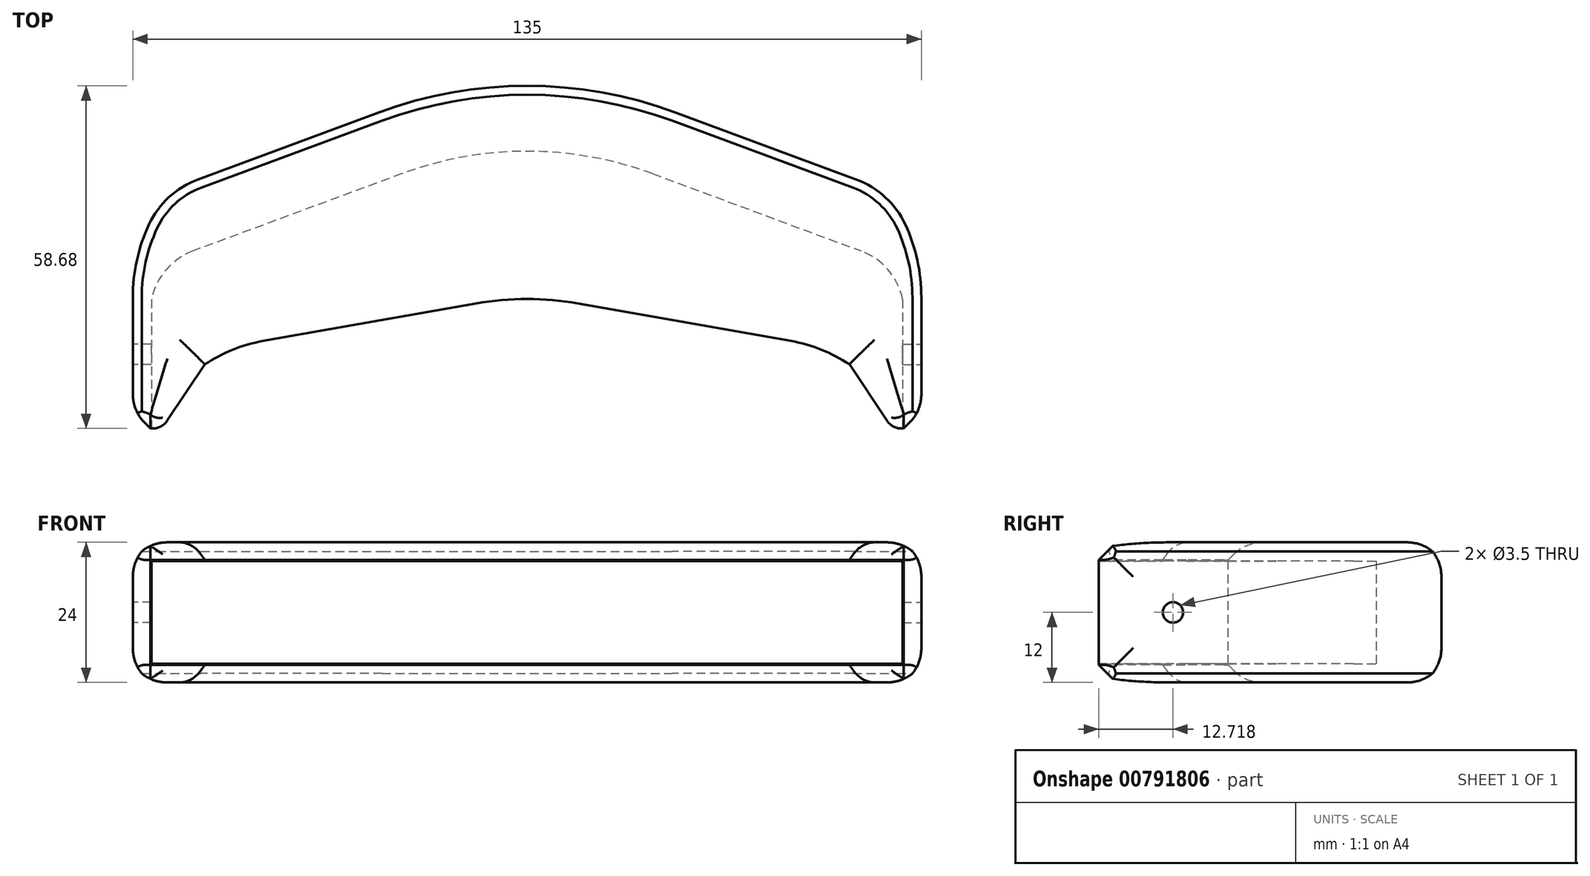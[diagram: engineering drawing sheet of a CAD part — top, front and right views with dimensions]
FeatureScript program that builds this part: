
annotation { "Feature Type Name" : "Feature", "Feature Type Description" : "" }
export const myFeature = defineFeature(function(context is Context, id is Id, definition is map)
    precondition{}
    {
        {
            var Q0;
            Q0=qCreatedBy(makeId("Top.planeOp"),FACE);
            var sketch = newSketch(context, id + "F0", { "sketchPlane" : qUnion([Q0])});
            skLineSegment(sketch, "E0.left", {"start": v(-67.5, -4.63) * mm, "end": v(-67.5, -27.07) * mm});
            skLineSegment(sketch, "E0.right", {"start": v(67.5, -4.63) * mm, "end": v(67.5, -27.07) * mm});
            skLineSegment(sketch, "E1", {"start": v(-22.58, 19.56) * mm, "end": v(-58.22, 6.36) * mm});
            skLineSegment(sketch, "E2", {"start": v(22.58, 19.56) * mm, "end": v(58.25, 6.35) * mm});
            skPoint(sketch, "E3.visualSharp", {"position": v(-67.5, 2.93) * mm});
            skPoint(sketch, "E4.visualSharp", {"position": v(67.5, 2.93) * mm});
            skPoint(sketch, "E5.visualSharp", {"position": v(0, 27.93) * mm});
            skArc(sketch, "E5.filletArc", {"start": v(22.58, 19.56) * mm, "mid": v(0, 23.61) * mm, "end": v(-22.58, 19.56) * mm});
            skLineSegment(sketch, "E6", {"start": v(-67.5, -27.07) * mm, "end": v(-64.1, -27.07) * mm});
            skLineSegment(sketch, "E7", {"start": v(-61.6, -25.74) * mm, "end": v(-55.17, -16.09) * mm});
            skLineSegment(sketch, "E8", {"start": v(67.5, -27.07) * mm, "end": v(64.1, -27.07) * mm});
            skLineSegment(sketch, "E9", {"start": v(61.6, -25.74) * mm, "end": v(55.17, -16.09) * mm});
            skPoint(sketch, "E10.visualSharp", {"position": v(-52.5, -12.08) * mm});
            skPoint(sketch, "E11.visualSharp", {"position": v(52.5, -12.08) * mm});
            skPoint(sketch, "E12.visualSharp", {"position": v(62.5, -27.07) * mm});
            skArc(sketch, "E12.filletArc", {"start": v(61.6, -25.74) * mm, "mid": v(62.69, -26.72) * mm, "end": v(64.1, -27.07) * mm});
            skPoint(sketch, "E13.visualSharp", {"position": v(-62.5, -27.07) * mm});
            skArc(sketch, "E13.filletArc", {"start": v(-64.1, -27.07) * mm, "mid": v(-62.69, -26.72) * mm, "end": v(-61.6, -25.74) * mm});
            skLineSegment(sketch, "E14", {"start": v(-45.18, -12.08) * mm, "end": v(-8.66, -5.66) * mm});
            skLineSegment(sketch, "E15", {"start": v(8.66, -5.66) * mm, "end": v(45.18, -12.08) * mm});
            skPoint(sketch, "E16.visualSharp", {"position": v(0, -4.13) * mm});
            skArc(sketch, "E16.filletArc", {"start": v(8.66, -5.66) * mm, "mid": v(0, -4.9) * mm, "end": v(-8.66, -5.66) * mm});
            skPoint(sketch, "E17.visualSharp", {"position": v(-63.32, 13.1) * mm});
            skPoint(sketch, "E18.visualSharp", {"position": v(58.32, 13.1) * mm});
            skArc(sketch, "E19", {"start": v(-58.22, 6.36) * mm, "mid": v(-64.3, 2.09) * mm, "end": v(-67.5, -4.63) * mm});
            skArc(sketch, "E20", {"start": v(67.5, -4.63) * mm, "mid": v(64.32, 2.08) * mm, "end": v(58.25, 6.35) * mm});
            skArc(sketch, "E21", {"start": v(-45.18, -12.08) * mm, "mid": v(-50.39, -13.57) * mm, "end": v(-55.17, -16.09) * mm});
            skArc(sketch, "E22", {"start": v(55.17, -16.09) * mm, "mid": v(50.39, -13.57) * mm, "end": v(45.18, -12.08) * mm});
            skPoint(sketch, "E23.visualSharp", {"position": v(-61, 13.86) * mm});
            skPoint(sketch, "E24.visualSharp", {"position": v(61.03, 13.85) * mm});
            skSolve(sketch);
        }
        {
            var Q0;
            Q0 = qSketchRegion(id + "F0", true);
            extrude(context, id + "F1", {"entities" : qUnion([Q0]), "depth" : 24 * mm, "offsetDistance" : 25 * mm});
        }
        {
            var Q0;
            Q0=makeQuery(id+"F1.opExtrude","SWEPT_FACE",FACE,{"disambiguationData":[OSD([sQuery(id+"F0.wireOp",EDGE,"E14")])]});
            var Q1;
            Q1=makeQuery(id+"F1.opExtrude","SWEPT_FACE",FACE,{"disambiguationData":[OSD([sQuery(id+"F0.wireOp",EDGE,"E16.filletArc")])]});
            var Q2;
            Q2=makeQuery(id+"F1.opExtrude","SWEPT_FACE",FACE,{"disambiguationData":[OSD([sQuery(id+"F0.wireOp",EDGE,"E15")])]});
            var Q3;
            Q3=makeQuery(id+"F1.opExtrude","SWEPT_FACE",FACE,{"disambiguationData":[OSD([sQuery(id+"F0.wireOp",EDGE,"E11.filletArc")])]});
            var Q4;
            Q4=makeQuery(id+"F1.opExtrude","SWEPT_FACE",FACE,{"disambiguationData":[OSD([sQuery(id+"F0.wireOp",EDGE,"E9")])]});
            var Q5;
            Q5=makeQuery(id+"F1.opExtrude","SWEPT_FACE",FACE,{"disambiguationData":[OSD([sQuery(id+"F0.wireOp",EDGE,"E12.filletArc")])]});
            var Q6;
            Q6=makeQuery(id+"F1.opExtrude","SWEPT_FACE",FACE,{"disambiguationData":[OSD([sQuery(id+"F0.wireOp",EDGE,"E7")])]});
            var Q7;
            Q7=makeQuery(id+"F1.opExtrude","SWEPT_FACE",FACE,{"disambiguationData":[OSD([sQuery(id+"F0.wireOp",EDGE,"E10.filletArc")])]});
            var Q8;
            Q8=makeQuery(id+"F1.opExtrude","SWEPT_FACE",FACE,{"disambiguationData":[OSD([sQuery(id+"F0.wireOp",EDGE,"E13.filletArc")])]});
            var Q9;
            Q9=makeQuery(id+"F1.opExtrude","SWEPT_FACE",FACE,{"disambiguationData":[OSD([sQuery(id+"F0.wireOp",EDGE,"E6")])]});
            var Q10;
            Q10=makeQuery(id+"F1.opExtrude","SWEPT_FACE",FACE,{"disambiguationData":[OSD([sQuery(id+"F0.wireOp",EDGE,"E8")])]});
            var Q11;
            Q11=makeQuery(id+"F1.opExtrude","SWEPT_FACE",FACE,{"disambiguationData":[OSD([sQuery(id+"F0.wireOp",EDGE,"E21")])]});
            var Q12;
            Q12=makeQuery(id+"F1.opExtrude","SWEPT_FACE",FACE,{"disambiguationData":[OSD([sQuery(id+"F0.wireOp",EDGE,"E22")])]});
            shell(context, id + "F2", {"entities" : qUnion([Q0, Q1, Q2, Q3, Q4, Q5, Q6, Q7, Q8, Q9, Q10, Q11, Q12]), "thickness" : 3.2 * mm});
        }
        {
            var Q0;
            Q0=makeQuery(id+"F1.opExtrude","CAP_FACE",FACE,{"disambiguationData":[OSD([sQuery(id+"F0.wireOp",EDGE,"E0.left"),sQuery(id+"F0.wireOp",EDGE,"E0.right"),sQuery(id+"F0.wireOp",EDGE,"E1"),sQuery(id+"F0.wireOp",EDGE,"E2"),sQuery(id+"F0.wireOp",EDGE,"E3.filletArc"),sQuery(id+"F0.wireOp",EDGE,"E4.filletArc"),sQuery(id+"F0.wireOp",EDGE,"E5.filletArc"),sQuery(id+"F0.wireOp",EDGE,"E6"),sQuery(id+"F0.wireOp",EDGE,"E7"),sQuery(id+"F0.wireOp",EDGE,"E8"),sQuery(id+"F0.wireOp",EDGE,"E9"),sQuery(id+"F0.wireOp",EDGE,"E10.filletArc"),sQuery(id+"F0.wireOp",EDGE,"E11.filletArc"),sQuery(id+"F0.wireOp",EDGE,"E12.filletArc"),sQuery(id+"F0.wireOp",EDGE,"E13.filletArc"),sQuery(id+"F0.wireOp",EDGE,"E14"),sQuery(id+"F0.wireOp",EDGE,"E15"),sQuery(id+"F0.wireOp",EDGE,"E16.filletArc")])],"isStart":false});
            var sketch = newSketch(context, id + "F3", { "sketchPlane" : qUnion([Q0])});
            skLineSegment(sketch, "E25.0", {"start": v(-25.35, 27.07) * mm, "end": v(-56.35, 15.59) * mm});
            skArc(sketch, "E25.1", {"start": v(25.35, 27.07) * mm, "mid": v(0, 31.61) * mm, "end": v(-25.35, 27.07) * mm});
            skLineSegment(sketch, "E25.2", {"start": v(25.35, 27.07) * mm, "end": v(56.36, 15.58) * mm});
            skArc(sketch, "E26", {"start": v(-64.73, 7.86) * mm, "mid": v(-66.8, 1.77) * mm, "end": v(-67.5, -4.63) * mm});
            skArc(sketch, "E27", {"start": v(67.5, -4.63) * mm, "mid": v(66.8, 1.74) * mm, "end": v(64.76, 7.82) * mm});
            skArc(sketch, "E28.filletArc", {"start": v(-56.35, 15.59) * mm, "mid": v(-61.3, 12.55) * mm, "end": v(-64.73, 7.86) * mm});
            skArc(sketch, "E29.filletArc", {"start": v(64.76, 7.82) * mm, "mid": v(61.33, 12.53) * mm, "end": v(56.36, 15.58) * mm});
            skLineSegment(sketch, "E30", {"start": v(-22.58, 19.56) * mm, "end": v(-58.22, 6.36) * mm});
            skLineSegment(sketch, "E31", {"start": v(22.58, 19.56) * mm, "end": v(58.25, 6.35) * mm});
            skArc(sketch, "E32.filletArc", {"start": v(22.58, 19.56) * mm, "mid": v(0, 23.61) * mm, "end": v(-22.58, 19.56) * mm});
            skArc(sketch, "E33", {"start": v(-58.22, 6.36) * mm, "mid": v(-64.3, 2.09) * mm, "end": v(-67.5, -4.63) * mm});
            skArc(sketch, "E34", {"start": v(67.5, -4.63) * mm, "mid": v(64.32, 2.08) * mm, "end": v(58.25, 6.35) * mm});
            skSolve(sketch);
        }
        {
            var Q0;
            Q0 = qSketchRegion(id + "F3", true);
            extrude(context, id + "F4", {"entities" : qUnion([Q0]), "operationType" : NewBodyOperationType.ADD, "oppositeDirection" : true, "depth" : 24 * mm, "offsetDistance" : 25 * mm});
        }
        {
            var Q0;
            Q0=makeQuery(id+"F4.boolean.opBoolean","MERGE",FACE,{"derivedFrom":[makeQuery(id+"F1.opExtrude","CAP_FACE",FACE,{"disambiguationData":[OSD([sQuery(id+"F0.wireOp",EDGE,"E0.left"),sQuery(id+"F0.wireOp",EDGE,"E0.right"),sQuery(id+"F0.wireOp",EDGE,"E1"),sQuery(id+"F0.wireOp",EDGE,"E2"),sQuery(id+"F0.wireOp",EDGE,"E3.filletArc"),sQuery(id+"F0.wireOp",EDGE,"E4.filletArc"),sQuery(id+"F0.wireOp",EDGE,"E5.filletArc"),sQuery(id+"F0.wireOp",EDGE,"E6"),sQuery(id+"F0.wireOp",EDGE,"E7"),sQuery(id+"F0.wireOp",EDGE,"E8"),sQuery(id+"F0.wireOp",EDGE,"E9"),sQuery(id+"F0.wireOp",EDGE,"E10.filletArc"),sQuery(id+"F0.wireOp",EDGE,"E11.filletArc"),sQuery(id+"F0.wireOp",EDGE,"E12.filletArc"),sQuery(id+"F0.wireOp",EDGE,"E13.filletArc"),sQuery(id+"F0.wireOp",EDGE,"E14"),sQuery(id+"F0.wireOp",EDGE,"E15"),sQuery(id+"F0.wireOp",EDGE,"E16.filletArc")])],"isStart":false}),makeQuery(id+"F4.opExtrude","CAP_FACE",FACE,{"disambiguationData":[OSD([sQuery(id+"F3.wireOp",EDGE,"276efb32-5cb6-4f63-bdc1-496fc01c60db.2"),sQuery(id+"F3.wireOp",EDGE,"276efb32-5cb6-4f63-bdc1-496fc01c60db.3"),sQuery(id+"F3.wireOp",EDGE,"276efb32-5cb6-4f63-bdc1-496fc01c60db.4"),sQuery(id+"F3.wireOp",EDGE,"0241c868-49d8-4b9a-ac46-58dfbb5efc39"),sQuery(id+"F3.wireOp",EDGE,"348bde47-0a47-42e3-8267-499f4a5522ae"),sQuery(id+"F3.wireOp",EDGE,"215ec280-f68a-4f47-a865-032d440a2936.filletArc"),sQuery(id+"F3.wireOp",EDGE,"fd759fa0-5ab4-4b6e-8cb0-b494d0b887aa.filletArc"),sQuery(id+"F3.wireOp",EDGE,"73b2d2fd-a5d6-4b7d-9539-ec2af92cbbd5"),sQuery(id+"F3.wireOp",EDGE,"2c1b0ead-8098-4b90-8860-aa6a1cb84409"),sQuery(id+"F3.wireOp",EDGE,"515ed680-fa81-4fbc-94c5-9d26c9a30982.filletArc"),sQuery(id+"F3.wireOp",EDGE,"67b69344-5ccb-49e4-9dbe-6815e7e981bc.filletArc"),sQuery(id+"F3.wireOp",EDGE,"a765c2de-9442-403f-932b-7ea1a12a6cac.filletArc")])],"isStart":true})]});
            var Q1;
            Q1=makeQuery(id+"F4.boolean.opBoolean","MERGE",FACE,{"derivedFrom":[makeQuery(id+"F1.opExtrude","CAP_FACE",FACE,{"disambiguationData":[OSD([sQuery(id+"F0.wireOp",EDGE,"E0.left"),sQuery(id+"F0.wireOp",EDGE,"E0.right"),sQuery(id+"F0.wireOp",EDGE,"E1"),sQuery(id+"F0.wireOp",EDGE,"E2"),sQuery(id+"F0.wireOp",EDGE,"E3.filletArc"),sQuery(id+"F0.wireOp",EDGE,"E4.filletArc"),sQuery(id+"F0.wireOp",EDGE,"E5.filletArc"),sQuery(id+"F0.wireOp",EDGE,"E6"),sQuery(id+"F0.wireOp",EDGE,"E7"),sQuery(id+"F0.wireOp",EDGE,"E8"),sQuery(id+"F0.wireOp",EDGE,"E9"),sQuery(id+"F0.wireOp",EDGE,"E10.filletArc"),sQuery(id+"F0.wireOp",EDGE,"E11.filletArc"),sQuery(id+"F0.wireOp",EDGE,"E12.filletArc"),sQuery(id+"F0.wireOp",EDGE,"E13.filletArc"),sQuery(id+"F0.wireOp",EDGE,"E14"),sQuery(id+"F0.wireOp",EDGE,"E15"),sQuery(id+"F0.wireOp",EDGE,"E16.filletArc")])],"isStart":true}),makeQuery(id+"F4.opExtrude","CAP_FACE",FACE,{"disambiguationData":[OSD([sQuery(id+"F3.wireOp",EDGE,"276efb32-5cb6-4f63-bdc1-496fc01c60db.2"),sQuery(id+"F3.wireOp",EDGE,"276efb32-5cb6-4f63-bdc1-496fc01c60db.3"),sQuery(id+"F3.wireOp",EDGE,"276efb32-5cb6-4f63-bdc1-496fc01c60db.4"),sQuery(id+"F3.wireOp",EDGE,"0241c868-49d8-4b9a-ac46-58dfbb5efc39"),sQuery(id+"F3.wireOp",EDGE,"348bde47-0a47-42e3-8267-499f4a5522ae"),sQuery(id+"F3.wireOp",EDGE,"215ec280-f68a-4f47-a865-032d440a2936.filletArc"),sQuery(id+"F3.wireOp",EDGE,"fd759fa0-5ab4-4b6e-8cb0-b494d0b887aa.filletArc"),sQuery(id+"F3.wireOp",EDGE,"73b2d2fd-a5d6-4b7d-9539-ec2af92cbbd5"),sQuery(id+"F3.wireOp",EDGE,"2c1b0ead-8098-4b90-8860-aa6a1cb84409"),sQuery(id+"F3.wireOp",EDGE,"515ed680-fa81-4fbc-94c5-9d26c9a30982.filletArc"),sQuery(id+"F3.wireOp",EDGE,"67b69344-5ccb-49e4-9dbe-6815e7e981bc.filletArc"),sQuery(id+"F3.wireOp",EDGE,"a765c2de-9442-403f-932b-7ea1a12a6cac.filletArc")])],"isStart":false})]});
            var Q2;
            Q2=makeQuery(id+"F1.opExtrude","SWEPT_EDGE",EDGE,{"disambiguationData":[OSD([sQuery(id+"F0.wireOp",EDGE,"E0.left"),sQuery(id+"F0.wireOp",EDGE,"E6")])]});
            var Q3;
            Q3=makeQuery(id+"F1.opExtrude","SWEPT_EDGE",EDGE,{"disambiguationData":[OSD([sQuery(id+"F0.wireOp",EDGE,"E0.right"),sQuery(id+"F0.wireOp",EDGE,"E8")])]});
            chamfer(context, id + "F5", {"entities" : qUnion([Q0, Q1, Q2, Q3]), "width" : 3 * mm, "tangentPropagation" : true});
        }
        {
            var Q0;
            Q0=makeQuery(id+"F1.opExtrude","SWEPT_FACE",FACE,{"disambiguationData":[OSD([sQuery(id+"F0.wireOp",EDGE,"E0.left")])]});
            var sketch = newSketch(context, id + "F6", { "sketchPlane" : qUnion([Q0])});
            skCircle(sketch, "E35", {"center": v(14.35, 12) * mm, "radius": 1.75 * mm});
            skPoint(sketch, "E36", {"position": v(14.35, 21) * mm});
            skPoint(sketch, "E37", {"position": v(24.07, 12) * mm});
            skSolve(sketch);
        }
        {
            var Q0;
            Q0 = qSketchRegion(id + "F6", true);
            extrude(context, id + "F7", {"entities" : qUnion([Q0]), "operationType" : NewBodyOperationType.REMOVE, "oppositeDirection" : true, "depth" : 5 * mm, "offsetDistance" : 25 * mm});
        }
        {
            var Q0;
            Q0=makeQuery(id+"F1.opExtrude","SWEPT_FACE",FACE,{"disambiguationData":[OSD([sQuery(id+"F0.wireOp",EDGE,"E0.right")])]});
            var sketch = newSketch(context, id + "F8", { "sketchPlane" : qUnion([Q0])});
            skCircle(sketch, "E38", {"center": v(-14.35, 12) * mm, "radius": 1.75 * mm});
            skPoint(sketch, "E39", {"position": v(-14.35, 21) * mm});
            skPoint(sketch, "E40", {"position": v(-24.07, 12) * mm});
            skSolve(sketch);
        }
        {
            var Q0;
            Q0 = qSketchRegion(id + "F8", true);
            extrude(context, id + "F9", {"entities" : qUnion([Q0]), "operationType" : NewBodyOperationType.REMOVE, "oppositeDirection" : true, "depth" : 5 * mm, "offsetDistance" : 25 * mm});
        }
        {
            var Q0;
            {var subQ0=sQuery(id+"F3.wireOp",EDGE,"E25.1");Q0=makeQuery(id+"F5.opChamfer","BLEND_EDGE",EDGE,{"blendedFrom":[makeQuery(id+"F4.opExtrude","CAP_EDGE",EDGE,{"disambiguationData":[OSD([subQ0])],"isStart":false}),makeQuery(id+"F4.opExtrude","SWEPT_FACE",FACE,{"disambiguationData":[OSD([subQ0])]})],"blendedInto":[makeQuery(id+"F4.opExtrude","SWEPT_FACE",FACE,{"disambiguationData":[OSD([subQ0])]})]});}
            var Q1;
            {var subQ0=sQuery(id+"F3.wireOp",EDGE,"E25.1");Q1=makeQuery(id+"F5.opChamfer","BLEND_EDGE",EDGE,{"blendedFrom":[makeQuery(id+"F4.opExtrude","CAP_EDGE",EDGE,{"disambiguationData":[OSD([subQ0])],"isStart":false}),makeQuery(id+"F4.boolean.opBoolean","MERGE",FACE,{"derivedFrom":[makeQuery(id+"F1.opExtrude","CAP_FACE",FACE,{"disambiguationData":[OSD([sQuery(id+"F0.wireOp",EDGE,"E0.left"),sQuery(id+"F0.wireOp",EDGE,"E0.right"),sQuery(id+"F0.wireOp",EDGE,"E1"),sQuery(id+"F0.wireOp",EDGE,"E2"),sQuery(id+"F0.wireOp",EDGE,"E5.filletArc"),sQuery(id+"F0.wireOp",EDGE,"E6"),sQuery(id+"F0.wireOp",EDGE,"E7"),sQuery(id+"F0.wireOp",EDGE,"E8"),sQuery(id+"F0.wireOp",EDGE,"E9"),sQuery(id+"F0.wireOp",EDGE,"E12.filletArc"),sQuery(id+"F0.wireOp",EDGE,"E13.filletArc"),sQuery(id+"F0.wireOp",EDGE,"E14"),sQuery(id+"F0.wireOp",EDGE,"E15"),sQuery(id+"F0.wireOp",EDGE,"E16.filletArc"),sQuery(id+"F0.wireOp",EDGE,"E19"),sQuery(id+"F0.wireOp",EDGE,"E20"),sQuery(id+"F0.wireOp",EDGE,"E21"),sQuery(id+"F0.wireOp",EDGE,"E22")])],"isStart":true}),makeQuery(id+"F4.opExtrude","CAP_FACE",FACE,{"disambiguationData":[OSD([sQuery(id+"F3.wireOp",EDGE,"E25.0"),subQ0,sQuery(id+"F3.wireOp",EDGE,"E25.2"),sQuery(id+"F3.wireOp",EDGE,"E26"),sQuery(id+"F3.wireOp",EDGE,"E27"),sQuery(id+"F3.wireOp",EDGE,"E28.filletArc"),sQuery(id+"F3.wireOp",EDGE,"E29.filletArc"),sQuery(id+"F3.wireOp",EDGE,"E30"),sQuery(id+"F3.wireOp",EDGE,"E31"),sQuery(id+"F3.wireOp",EDGE,"E32.filletArc"),sQuery(id+"F3.wireOp",EDGE,"E33"),sQuery(id+"F3.wireOp",EDGE,"E34")])],"isStart":false})]})],"blendedInto":[makeQuery(id+"F4.boolean.opBoolean","MERGE",FACE,{"derivedFrom":[makeQuery(id+"F1.opExtrude","CAP_FACE",FACE,{"disambiguationData":[OSD([sQuery(id+"F0.wireOp",EDGE,"E0.left"),sQuery(id+"F0.wireOp",EDGE,"E0.right"),sQuery(id+"F0.wireOp",EDGE,"E1"),sQuery(id+"F0.wireOp",EDGE,"E2"),sQuery(id+"F0.wireOp",EDGE,"E5.filletArc"),sQuery(id+"F0.wireOp",EDGE,"E6"),sQuery(id+"F0.wireOp",EDGE,"E7"),sQuery(id+"F0.wireOp",EDGE,"E8"),sQuery(id+"F0.wireOp",EDGE,"E9"),sQuery(id+"F0.wireOp",EDGE,"E12.filletArc"),sQuery(id+"F0.wireOp",EDGE,"E13.filletArc"),sQuery(id+"F0.wireOp",EDGE,"E14"),sQuery(id+"F0.wireOp",EDGE,"E15"),sQuery(id+"F0.wireOp",EDGE,"E16.filletArc"),sQuery(id+"F0.wireOp",EDGE,"E19"),sQuery(id+"F0.wireOp",EDGE,"E20"),sQuery(id+"F0.wireOp",EDGE,"E21"),sQuery(id+"F0.wireOp",EDGE,"E22")])],"isStart":true}),makeQuery(id+"F4.opExtrude","CAP_FACE",FACE,{"disambiguationData":[OSD([sQuery(id+"F3.wireOp",EDGE,"E25.0"),subQ0,sQuery(id+"F3.wireOp",EDGE,"E25.2"),sQuery(id+"F3.wireOp",EDGE,"E26"),sQuery(id+"F3.wireOp",EDGE,"E27"),sQuery(id+"F3.wireOp",EDGE,"E28.filletArc"),sQuery(id+"F3.wireOp",EDGE,"E29.filletArc"),sQuery(id+"F3.wireOp",EDGE,"E30"),sQuery(id+"F3.wireOp",EDGE,"E31"),sQuery(id+"F3.wireOp",EDGE,"E32.filletArc"),sQuery(id+"F3.wireOp",EDGE,"E33"),sQuery(id+"F3.wireOp",EDGE,"E34")])],"isStart":false})]})]});}
            var Q2;
            {var subQ0=sQuery(id+"F3.wireOp",EDGE,"E25.0");Q2=makeQuery(id+"F5.opChamfer","BLEND_EDGE",EDGE,{"blendedFrom":[makeQuery(id+"F4.opExtrude","CAP_EDGE",EDGE,{"disambiguationData":[OSD([subQ0])],"isStart":true}),makeQuery(id+"F4.boolean.opBoolean","MERGE",FACE,{"derivedFrom":[makeQuery(id+"F1.opExtrude","CAP_FACE",FACE,{"disambiguationData":[OSD([sQuery(id+"F0.wireOp",EDGE,"E0.left"),sQuery(id+"F0.wireOp",EDGE,"E0.right"),sQuery(id+"F0.wireOp",EDGE,"E1"),sQuery(id+"F0.wireOp",EDGE,"E2"),sQuery(id+"F0.wireOp",EDGE,"E5.filletArc"),sQuery(id+"F0.wireOp",EDGE,"E6"),sQuery(id+"F0.wireOp",EDGE,"E7"),sQuery(id+"F0.wireOp",EDGE,"E8"),sQuery(id+"F0.wireOp",EDGE,"E9"),sQuery(id+"F0.wireOp",EDGE,"E12.filletArc"),sQuery(id+"F0.wireOp",EDGE,"E13.filletArc"),sQuery(id+"F0.wireOp",EDGE,"E14"),sQuery(id+"F0.wireOp",EDGE,"E15"),sQuery(id+"F0.wireOp",EDGE,"E16.filletArc"),sQuery(id+"F0.wireOp",EDGE,"E19"),sQuery(id+"F0.wireOp",EDGE,"E20"),sQuery(id+"F0.wireOp",EDGE,"E21"),sQuery(id+"F0.wireOp",EDGE,"E22")])],"isStart":false}),makeQuery(id+"F4.opExtrude","CAP_FACE",FACE,{"disambiguationData":[OSD([subQ0,sQuery(id+"F3.wireOp",EDGE,"E25.1"),sQuery(id+"F3.wireOp",EDGE,"E25.2"),sQuery(id+"F3.wireOp",EDGE,"E26"),sQuery(id+"F3.wireOp",EDGE,"E27"),sQuery(id+"F3.wireOp",EDGE,"E28.filletArc"),sQuery(id+"F3.wireOp",EDGE,"E29.filletArc"),sQuery(id+"F3.wireOp",EDGE,"E30"),sQuery(id+"F3.wireOp",EDGE,"E31"),sQuery(id+"F3.wireOp",EDGE,"E32.filletArc"),sQuery(id+"F3.wireOp",EDGE,"E33"),sQuery(id+"F3.wireOp",EDGE,"E34")])],"isStart":true})]})],"blendedInto":[makeQuery(id+"F4.boolean.opBoolean","MERGE",FACE,{"derivedFrom":[makeQuery(id+"F1.opExtrude","CAP_FACE",FACE,{"disambiguationData":[OSD([sQuery(id+"F0.wireOp",EDGE,"E0.left"),sQuery(id+"F0.wireOp",EDGE,"E0.right"),sQuery(id+"F0.wireOp",EDGE,"E1"),sQuery(id+"F0.wireOp",EDGE,"E2"),sQuery(id+"F0.wireOp",EDGE,"E5.filletArc"),sQuery(id+"F0.wireOp",EDGE,"E6"),sQuery(id+"F0.wireOp",EDGE,"E7"),sQuery(id+"F0.wireOp",EDGE,"E8"),sQuery(id+"F0.wireOp",EDGE,"E9"),sQuery(id+"F0.wireOp",EDGE,"E12.filletArc"),sQuery(id+"F0.wireOp",EDGE,"E13.filletArc"),sQuery(id+"F0.wireOp",EDGE,"E14"),sQuery(id+"F0.wireOp",EDGE,"E15"),sQuery(id+"F0.wireOp",EDGE,"E16.filletArc"),sQuery(id+"F0.wireOp",EDGE,"E19"),sQuery(id+"F0.wireOp",EDGE,"E20"),sQuery(id+"F0.wireOp",EDGE,"E21"),sQuery(id+"F0.wireOp",EDGE,"E22")])],"isStart":false}),makeQuery(id+"F4.opExtrude","CAP_FACE",FACE,{"disambiguationData":[OSD([subQ0,sQuery(id+"F3.wireOp",EDGE,"E25.1"),sQuery(id+"F3.wireOp",EDGE,"E25.2"),sQuery(id+"F3.wireOp",EDGE,"E26"),sQuery(id+"F3.wireOp",EDGE,"E27"),sQuery(id+"F3.wireOp",EDGE,"E28.filletArc"),sQuery(id+"F3.wireOp",EDGE,"E29.filletArc"),sQuery(id+"F3.wireOp",EDGE,"E30"),sQuery(id+"F3.wireOp",EDGE,"E31"),sQuery(id+"F3.wireOp",EDGE,"E32.filletArc"),sQuery(id+"F3.wireOp",EDGE,"E33"),sQuery(id+"F3.wireOp",EDGE,"E34")])],"isStart":true})]})]});}
            var Q3;
            {var subQ0=sQuery(id+"F3.wireOp",EDGE,"E25.0");Q3=makeQuery(id+"F5.opChamfer","BLEND_EDGE",EDGE,{"blendedFrom":[makeQuery(id+"F4.opExtrude","CAP_EDGE",EDGE,{"disambiguationData":[OSD([subQ0])],"isStart":true}),makeQuery(id+"F4.opExtrude","SWEPT_FACE",FACE,{"disambiguationData":[OSD([subQ0])]})],"blendedInto":[makeQuery(id+"F4.opExtrude","SWEPT_FACE",FACE,{"disambiguationData":[OSD([subQ0])]})]});}
            var Q4;
            {var subQ0=sQuery(id+"F0.wireOp",EDGE,"E0.right");Q4=makeQuery(id+"F5.opChamfer","BLEND_EDGE",EDGE,{"blendedFrom":[makeQuery(id+"F1.opExtrude","SWEPT_EDGE",EDGE,{"disambiguationData":[OSD([subQ0,sQuery(id+"F0.wireOp",EDGE,"E8")])]}),makeQuery(id+"F1.opExtrude","SWEPT_FACE",FACE,{"disambiguationData":[OSD([subQ0])]})],"blendedInto":[makeQuery(id+"F1.opExtrude","SWEPT_FACE",FACE,{"disambiguationData":[OSD([subQ0])]})]});}
            var Q5;
            {var subQ0=sQuery(id+"F0.wireOp",EDGE,"E0.left");Q5=makeQuery(id+"F5.opChamfer","BLEND_EDGE",EDGE,{"blendedFrom":[makeQuery(id+"F1.opExtrude","SWEPT_EDGE",EDGE,{"disambiguationData":[OSD([subQ0,sQuery(id+"F0.wireOp",EDGE,"E6")])]}),makeQuery(id+"F1.opExtrude","SWEPT_FACE",FACE,{"disambiguationData":[OSD([subQ0])]})],"blendedInto":[makeQuery(id+"F1.opExtrude","SWEPT_FACE",FACE,{"disambiguationData":[OSD([subQ0])]})]});}
            var Q6;
            {var subQ0=sQuery(id+"F0.wireOp",EDGE,"E15");Q6=makeQuery(id+"F5.opChamfer","BLEND_EDGE",EDGE,{"blendedFrom":[makeQuery(id+"F1.opExtrude","CAP_EDGE",EDGE,{"disambiguationData":[OSD([subQ0])],"isStart":false}),makeQuery(id+"F4.boolean.opBoolean","MERGE",FACE,{"derivedFrom":[makeQuery(id+"F1.opExtrude","CAP_FACE",FACE,{"disambiguationData":[OSD([sQuery(id+"F0.wireOp",EDGE,"E0.left"),sQuery(id+"F0.wireOp",EDGE,"E0.right"),sQuery(id+"F0.wireOp",EDGE,"E1"),sQuery(id+"F0.wireOp",EDGE,"E2"),sQuery(id+"F0.wireOp",EDGE,"E5.filletArc"),sQuery(id+"F0.wireOp",EDGE,"E6"),sQuery(id+"F0.wireOp",EDGE,"E7"),sQuery(id+"F0.wireOp",EDGE,"E8"),sQuery(id+"F0.wireOp",EDGE,"E9"),sQuery(id+"F0.wireOp",EDGE,"E12.filletArc"),sQuery(id+"F0.wireOp",EDGE,"E13.filletArc"),sQuery(id+"F0.wireOp",EDGE,"E14"),subQ0,sQuery(id+"F0.wireOp",EDGE,"E16.filletArc"),sQuery(id+"F0.wireOp",EDGE,"E19"),sQuery(id+"F0.wireOp",EDGE,"E20"),sQuery(id+"F0.wireOp",EDGE,"E21"),sQuery(id+"F0.wireOp",EDGE,"E22")])],"isStart":false}),makeQuery(id+"F4.opExtrude","CAP_FACE",FACE,{"disambiguationData":[OSD([sQuery(id+"F3.wireOp",EDGE,"E25.0"),sQuery(id+"F3.wireOp",EDGE,"E25.1"),sQuery(id+"F3.wireOp",EDGE,"E25.2"),sQuery(id+"F3.wireOp",EDGE,"E26"),sQuery(id+"F3.wireOp",EDGE,"E27"),sQuery(id+"F3.wireOp",EDGE,"E28.filletArc"),sQuery(id+"F3.wireOp",EDGE,"E29.filletArc"),sQuery(id+"F3.wireOp",EDGE,"E30"),sQuery(id+"F3.wireOp",EDGE,"E31"),sQuery(id+"F3.wireOp",EDGE,"E32.filletArc"),sQuery(id+"F3.wireOp",EDGE,"E33"),sQuery(id+"F3.wireOp",EDGE,"E34")])],"isStart":true})]})],"blendedInto":[makeQuery(id+"F4.boolean.opBoolean","MERGE",FACE,{"derivedFrom":[makeQuery(id+"F1.opExtrude","CAP_FACE",FACE,{"disambiguationData":[OSD([sQuery(id+"F0.wireOp",EDGE,"E0.left"),sQuery(id+"F0.wireOp",EDGE,"E0.right"),sQuery(id+"F0.wireOp",EDGE,"E1"),sQuery(id+"F0.wireOp",EDGE,"E2"),sQuery(id+"F0.wireOp",EDGE,"E5.filletArc"),sQuery(id+"F0.wireOp",EDGE,"E6"),sQuery(id+"F0.wireOp",EDGE,"E7"),sQuery(id+"F0.wireOp",EDGE,"E8"),sQuery(id+"F0.wireOp",EDGE,"E9"),sQuery(id+"F0.wireOp",EDGE,"E12.filletArc"),sQuery(id+"F0.wireOp",EDGE,"E13.filletArc"),sQuery(id+"F0.wireOp",EDGE,"E14"),subQ0,sQuery(id+"F0.wireOp",EDGE,"E16.filletArc"),sQuery(id+"F0.wireOp",EDGE,"E19"),sQuery(id+"F0.wireOp",EDGE,"E20"),sQuery(id+"F0.wireOp",EDGE,"E21"),sQuery(id+"F0.wireOp",EDGE,"E22")])],"isStart":false}),makeQuery(id+"F4.opExtrude","CAP_FACE",FACE,{"disambiguationData":[OSD([sQuery(id+"F3.wireOp",EDGE,"E25.0"),sQuery(id+"F3.wireOp",EDGE,"E25.1"),sQuery(id+"F3.wireOp",EDGE,"E25.2"),sQuery(id+"F3.wireOp",EDGE,"E26"),sQuery(id+"F3.wireOp",EDGE,"E27"),sQuery(id+"F3.wireOp",EDGE,"E28.filletArc"),sQuery(id+"F3.wireOp",EDGE,"E29.filletArc"),sQuery(id+"F3.wireOp",EDGE,"E30"),sQuery(id+"F3.wireOp",EDGE,"E31"),sQuery(id+"F3.wireOp",EDGE,"E32.filletArc"),sQuery(id+"F3.wireOp",EDGE,"E33"),sQuery(id+"F3.wireOp",EDGE,"E34")])],"isStart":true})]})]});}
            var Q7;
            {var subQ0=sQuery(id+"F0.wireOp",EDGE,"E9");Q7=makeQuery(id+"F5.opChamfer","BLEND_EDGE",EDGE,{"blendedFrom":[makeQuery(id+"F1.opExtrude","CAP_EDGE",EDGE,{"disambiguationData":[OSD([subQ0])],"isStart":false}),makeQuery(id+"F4.boolean.opBoolean","MERGE",FACE,{"derivedFrom":[makeQuery(id+"F1.opExtrude","CAP_FACE",FACE,{"disambiguationData":[OSD([sQuery(id+"F0.wireOp",EDGE,"E0.left"),sQuery(id+"F0.wireOp",EDGE,"E0.right"),sQuery(id+"F0.wireOp",EDGE,"E1"),sQuery(id+"F0.wireOp",EDGE,"E2"),sQuery(id+"F0.wireOp",EDGE,"E5.filletArc"),sQuery(id+"F0.wireOp",EDGE,"E6"),sQuery(id+"F0.wireOp",EDGE,"E7"),sQuery(id+"F0.wireOp",EDGE,"E8"),subQ0,sQuery(id+"F0.wireOp",EDGE,"E12.filletArc"),sQuery(id+"F0.wireOp",EDGE,"E13.filletArc"),sQuery(id+"F0.wireOp",EDGE,"E14"),sQuery(id+"F0.wireOp",EDGE,"E15"),sQuery(id+"F0.wireOp",EDGE,"E16.filletArc"),sQuery(id+"F0.wireOp",EDGE,"E19"),sQuery(id+"F0.wireOp",EDGE,"E20"),sQuery(id+"F0.wireOp",EDGE,"E21"),sQuery(id+"F0.wireOp",EDGE,"E22")])],"isStart":false}),makeQuery(id+"F4.opExtrude","CAP_FACE",FACE,{"disambiguationData":[OSD([sQuery(id+"F3.wireOp",EDGE,"E25.0"),sQuery(id+"F3.wireOp",EDGE,"E25.1"),sQuery(id+"F3.wireOp",EDGE,"E25.2"),sQuery(id+"F3.wireOp",EDGE,"E26"),sQuery(id+"F3.wireOp",EDGE,"E27"),sQuery(id+"F3.wireOp",EDGE,"E28.filletArc"),sQuery(id+"F3.wireOp",EDGE,"E29.filletArc"),sQuery(id+"F3.wireOp",EDGE,"E30"),sQuery(id+"F3.wireOp",EDGE,"E31"),sQuery(id+"F3.wireOp",EDGE,"E32.filletArc"),sQuery(id+"F3.wireOp",EDGE,"E33"),sQuery(id+"F3.wireOp",EDGE,"E34")])],"isStart":true})]})],"blendedInto":[makeQuery(id+"F4.boolean.opBoolean","MERGE",FACE,{"derivedFrom":[makeQuery(id+"F1.opExtrude","CAP_FACE",FACE,{"disambiguationData":[OSD([sQuery(id+"F0.wireOp",EDGE,"E0.left"),sQuery(id+"F0.wireOp",EDGE,"E0.right"),sQuery(id+"F0.wireOp",EDGE,"E1"),sQuery(id+"F0.wireOp",EDGE,"E2"),sQuery(id+"F0.wireOp",EDGE,"E5.filletArc"),sQuery(id+"F0.wireOp",EDGE,"E6"),sQuery(id+"F0.wireOp",EDGE,"E7"),sQuery(id+"F0.wireOp",EDGE,"E8"),subQ0,sQuery(id+"F0.wireOp",EDGE,"E12.filletArc"),sQuery(id+"F0.wireOp",EDGE,"E13.filletArc"),sQuery(id+"F0.wireOp",EDGE,"E14"),sQuery(id+"F0.wireOp",EDGE,"E15"),sQuery(id+"F0.wireOp",EDGE,"E16.filletArc"),sQuery(id+"F0.wireOp",EDGE,"E19"),sQuery(id+"F0.wireOp",EDGE,"E20"),sQuery(id+"F0.wireOp",EDGE,"E21"),sQuery(id+"F0.wireOp",EDGE,"E22")])],"isStart":false}),makeQuery(id+"F4.opExtrude","CAP_FACE",FACE,{"disambiguationData":[OSD([sQuery(id+"F3.wireOp",EDGE,"E25.0"),sQuery(id+"F3.wireOp",EDGE,"E25.1"),sQuery(id+"F3.wireOp",EDGE,"E25.2"),sQuery(id+"F3.wireOp",EDGE,"E26"),sQuery(id+"F3.wireOp",EDGE,"E27"),sQuery(id+"F3.wireOp",EDGE,"E28.filletArc"),sQuery(id+"F3.wireOp",EDGE,"E29.filletArc"),sQuery(id+"F3.wireOp",EDGE,"E30"),sQuery(id+"F3.wireOp",EDGE,"E31"),sQuery(id+"F3.wireOp",EDGE,"E32.filletArc"),sQuery(id+"F3.wireOp",EDGE,"E33"),sQuery(id+"F3.wireOp",EDGE,"E34")])],"isStart":true})]})]});}
            var Q8;
            {var subQ0=sQuery(id+"F0.wireOp",EDGE,"E7");Q8=makeQuery(id+"F5.opChamfer","BLEND_EDGE",EDGE,{"blendedFrom":[makeQuery(id+"F1.opExtrude","CAP_EDGE",EDGE,{"disambiguationData":[OSD([subQ0])],"isStart":false}),makeQuery(id+"F4.boolean.opBoolean","MERGE",FACE,{"derivedFrom":[makeQuery(id+"F1.opExtrude","CAP_FACE",FACE,{"disambiguationData":[OSD([sQuery(id+"F0.wireOp",EDGE,"E0.left"),sQuery(id+"F0.wireOp",EDGE,"E0.right"),sQuery(id+"F0.wireOp",EDGE,"E1"),sQuery(id+"F0.wireOp",EDGE,"E2"),sQuery(id+"F0.wireOp",EDGE,"E5.filletArc"),sQuery(id+"F0.wireOp",EDGE,"E6"),subQ0,sQuery(id+"F0.wireOp",EDGE,"E8"),sQuery(id+"F0.wireOp",EDGE,"E9"),sQuery(id+"F0.wireOp",EDGE,"E12.filletArc"),sQuery(id+"F0.wireOp",EDGE,"E13.filletArc"),sQuery(id+"F0.wireOp",EDGE,"E14"),sQuery(id+"F0.wireOp",EDGE,"E15"),sQuery(id+"F0.wireOp",EDGE,"E16.filletArc"),sQuery(id+"F0.wireOp",EDGE,"E19"),sQuery(id+"F0.wireOp",EDGE,"E20"),sQuery(id+"F0.wireOp",EDGE,"E21"),sQuery(id+"F0.wireOp",EDGE,"E22")])],"isStart":false}),makeQuery(id+"F4.opExtrude","CAP_FACE",FACE,{"disambiguationData":[OSD([sQuery(id+"F3.wireOp",EDGE,"E25.0"),sQuery(id+"F3.wireOp",EDGE,"E25.1"),sQuery(id+"F3.wireOp",EDGE,"E25.2"),sQuery(id+"F3.wireOp",EDGE,"E26"),sQuery(id+"F3.wireOp",EDGE,"E27"),sQuery(id+"F3.wireOp",EDGE,"E28.filletArc"),sQuery(id+"F3.wireOp",EDGE,"E29.filletArc"),sQuery(id+"F3.wireOp",EDGE,"E30"),sQuery(id+"F3.wireOp",EDGE,"E31"),sQuery(id+"F3.wireOp",EDGE,"E32.filletArc"),sQuery(id+"F3.wireOp",EDGE,"E33"),sQuery(id+"F3.wireOp",EDGE,"E34")])],"isStart":true})]})],"blendedInto":[makeQuery(id+"F4.boolean.opBoolean","MERGE",FACE,{"derivedFrom":[makeQuery(id+"F1.opExtrude","CAP_FACE",FACE,{"disambiguationData":[OSD([sQuery(id+"F0.wireOp",EDGE,"E0.left"),sQuery(id+"F0.wireOp",EDGE,"E0.right"),sQuery(id+"F0.wireOp",EDGE,"E1"),sQuery(id+"F0.wireOp",EDGE,"E2"),sQuery(id+"F0.wireOp",EDGE,"E5.filletArc"),sQuery(id+"F0.wireOp",EDGE,"E6"),subQ0,sQuery(id+"F0.wireOp",EDGE,"E8"),sQuery(id+"F0.wireOp",EDGE,"E9"),sQuery(id+"F0.wireOp",EDGE,"E12.filletArc"),sQuery(id+"F0.wireOp",EDGE,"E13.filletArc"),sQuery(id+"F0.wireOp",EDGE,"E14"),sQuery(id+"F0.wireOp",EDGE,"E15"),sQuery(id+"F0.wireOp",EDGE,"E16.filletArc"),sQuery(id+"F0.wireOp",EDGE,"E19"),sQuery(id+"F0.wireOp",EDGE,"E20"),sQuery(id+"F0.wireOp",EDGE,"E21"),sQuery(id+"F0.wireOp",EDGE,"E22")])],"isStart":false}),makeQuery(id+"F4.opExtrude","CAP_FACE",FACE,{"disambiguationData":[OSD([sQuery(id+"F3.wireOp",EDGE,"E25.0"),sQuery(id+"F3.wireOp",EDGE,"E25.1"),sQuery(id+"F3.wireOp",EDGE,"E25.2"),sQuery(id+"F3.wireOp",EDGE,"E26"),sQuery(id+"F3.wireOp",EDGE,"E27"),sQuery(id+"F3.wireOp",EDGE,"E28.filletArc"),sQuery(id+"F3.wireOp",EDGE,"E29.filletArc"),sQuery(id+"F3.wireOp",EDGE,"E30"),sQuery(id+"F3.wireOp",EDGE,"E31"),sQuery(id+"F3.wireOp",EDGE,"E32.filletArc"),sQuery(id+"F3.wireOp",EDGE,"E33"),sQuery(id+"F3.wireOp",EDGE,"E34")])],"isStart":true})]})]});}
            var Q9;
            {var subQ0=sQuery(id+"F0.wireOp",EDGE,"E14");Q9=makeQuery(id+"F5.opChamfer","BLEND_EDGE",EDGE,{"blendedFrom":[makeQuery(id+"F1.opExtrude","CAP_EDGE",EDGE,{"disambiguationData":[OSD([subQ0])],"isStart":true}),makeQuery(id+"F4.boolean.opBoolean","MERGE",FACE,{"derivedFrom":[makeQuery(id+"F1.opExtrude","CAP_FACE",FACE,{"disambiguationData":[OSD([sQuery(id+"F0.wireOp",EDGE,"E0.left"),sQuery(id+"F0.wireOp",EDGE,"E0.right"),sQuery(id+"F0.wireOp",EDGE,"E1"),sQuery(id+"F0.wireOp",EDGE,"E2"),sQuery(id+"F0.wireOp",EDGE,"E5.filletArc"),sQuery(id+"F0.wireOp",EDGE,"E6"),sQuery(id+"F0.wireOp",EDGE,"E7"),sQuery(id+"F0.wireOp",EDGE,"E8"),sQuery(id+"F0.wireOp",EDGE,"E9"),sQuery(id+"F0.wireOp",EDGE,"E12.filletArc"),sQuery(id+"F0.wireOp",EDGE,"E13.filletArc"),subQ0,sQuery(id+"F0.wireOp",EDGE,"E15"),sQuery(id+"F0.wireOp",EDGE,"E16.filletArc"),sQuery(id+"F0.wireOp",EDGE,"E19"),sQuery(id+"F0.wireOp",EDGE,"E20"),sQuery(id+"F0.wireOp",EDGE,"E21"),sQuery(id+"F0.wireOp",EDGE,"E22")])],"isStart":true}),makeQuery(id+"F4.opExtrude","CAP_FACE",FACE,{"disambiguationData":[OSD([sQuery(id+"F3.wireOp",EDGE,"E25.0"),sQuery(id+"F3.wireOp",EDGE,"E25.1"),sQuery(id+"F3.wireOp",EDGE,"E25.2"),sQuery(id+"F3.wireOp",EDGE,"E26"),sQuery(id+"F3.wireOp",EDGE,"E27"),sQuery(id+"F3.wireOp",EDGE,"E28.filletArc"),sQuery(id+"F3.wireOp",EDGE,"E29.filletArc"),sQuery(id+"F3.wireOp",EDGE,"E30"),sQuery(id+"F3.wireOp",EDGE,"E31"),sQuery(id+"F3.wireOp",EDGE,"E32.filletArc"),sQuery(id+"F3.wireOp",EDGE,"E33"),sQuery(id+"F3.wireOp",EDGE,"E34")])],"isStart":false})]})],"blendedInto":[makeQuery(id+"F4.boolean.opBoolean","MERGE",FACE,{"derivedFrom":[makeQuery(id+"F1.opExtrude","CAP_FACE",FACE,{"disambiguationData":[OSD([sQuery(id+"F0.wireOp",EDGE,"E0.left"),sQuery(id+"F0.wireOp",EDGE,"E0.right"),sQuery(id+"F0.wireOp",EDGE,"E1"),sQuery(id+"F0.wireOp",EDGE,"E2"),sQuery(id+"F0.wireOp",EDGE,"E5.filletArc"),sQuery(id+"F0.wireOp",EDGE,"E6"),sQuery(id+"F0.wireOp",EDGE,"E7"),sQuery(id+"F0.wireOp",EDGE,"E8"),sQuery(id+"F0.wireOp",EDGE,"E9"),sQuery(id+"F0.wireOp",EDGE,"E12.filletArc"),sQuery(id+"F0.wireOp",EDGE,"E13.filletArc"),subQ0,sQuery(id+"F0.wireOp",EDGE,"E15"),sQuery(id+"F0.wireOp",EDGE,"E16.filletArc"),sQuery(id+"F0.wireOp",EDGE,"E19"),sQuery(id+"F0.wireOp",EDGE,"E20"),sQuery(id+"F0.wireOp",EDGE,"E21"),sQuery(id+"F0.wireOp",EDGE,"E22")])],"isStart":true}),makeQuery(id+"F4.opExtrude","CAP_FACE",FACE,{"disambiguationData":[OSD([sQuery(id+"F3.wireOp",EDGE,"E25.0"),sQuery(id+"F3.wireOp",EDGE,"E25.1"),sQuery(id+"F3.wireOp",EDGE,"E25.2"),sQuery(id+"F3.wireOp",EDGE,"E26"),sQuery(id+"F3.wireOp",EDGE,"E27"),sQuery(id+"F3.wireOp",EDGE,"E28.filletArc"),sQuery(id+"F3.wireOp",EDGE,"E29.filletArc"),sQuery(id+"F3.wireOp",EDGE,"E30"),sQuery(id+"F3.wireOp",EDGE,"E31"),sQuery(id+"F3.wireOp",EDGE,"E32.filletArc"),sQuery(id+"F3.wireOp",EDGE,"E33"),sQuery(id+"F3.wireOp",EDGE,"E34")])],"isStart":false})]})]});}
            var Q10;
            {var subQ0=sQuery(id+"F0.wireOp",EDGE,"E9");Q10=makeQuery(id+"F5.opChamfer","BLEND_EDGE",EDGE,{"blendedFrom":[makeQuery(id+"F1.opExtrude","CAP_EDGE",EDGE,{"disambiguationData":[OSD([subQ0])],"isStart":true}),makeQuery(id+"F4.boolean.opBoolean","MERGE",FACE,{"derivedFrom":[makeQuery(id+"F1.opExtrude","CAP_FACE",FACE,{"disambiguationData":[OSD([sQuery(id+"F0.wireOp",EDGE,"E0.left"),sQuery(id+"F0.wireOp",EDGE,"E0.right"),sQuery(id+"F0.wireOp",EDGE,"E1"),sQuery(id+"F0.wireOp",EDGE,"E2"),sQuery(id+"F0.wireOp",EDGE,"E5.filletArc"),sQuery(id+"F0.wireOp",EDGE,"E6"),sQuery(id+"F0.wireOp",EDGE,"E7"),sQuery(id+"F0.wireOp",EDGE,"E8"),subQ0,sQuery(id+"F0.wireOp",EDGE,"E12.filletArc"),sQuery(id+"F0.wireOp",EDGE,"E13.filletArc"),sQuery(id+"F0.wireOp",EDGE,"E14"),sQuery(id+"F0.wireOp",EDGE,"E15"),sQuery(id+"F0.wireOp",EDGE,"E16.filletArc"),sQuery(id+"F0.wireOp",EDGE,"E19"),sQuery(id+"F0.wireOp",EDGE,"E20"),sQuery(id+"F0.wireOp",EDGE,"E21"),sQuery(id+"F0.wireOp",EDGE,"E22")])],"isStart":true}),makeQuery(id+"F4.opExtrude","CAP_FACE",FACE,{"disambiguationData":[OSD([sQuery(id+"F3.wireOp",EDGE,"E25.0"),sQuery(id+"F3.wireOp",EDGE,"E25.1"),sQuery(id+"F3.wireOp",EDGE,"E25.2"),sQuery(id+"F3.wireOp",EDGE,"E26"),sQuery(id+"F3.wireOp",EDGE,"E27"),sQuery(id+"F3.wireOp",EDGE,"E28.filletArc"),sQuery(id+"F3.wireOp",EDGE,"E29.filletArc"),sQuery(id+"F3.wireOp",EDGE,"E30"),sQuery(id+"F3.wireOp",EDGE,"E31"),sQuery(id+"F3.wireOp",EDGE,"E32.filletArc"),sQuery(id+"F3.wireOp",EDGE,"E33"),sQuery(id+"F3.wireOp",EDGE,"E34")])],"isStart":false})]})],"blendedInto":[makeQuery(id+"F4.boolean.opBoolean","MERGE",FACE,{"derivedFrom":[makeQuery(id+"F1.opExtrude","CAP_FACE",FACE,{"disambiguationData":[OSD([sQuery(id+"F0.wireOp",EDGE,"E0.left"),sQuery(id+"F0.wireOp",EDGE,"E0.right"),sQuery(id+"F0.wireOp",EDGE,"E1"),sQuery(id+"F0.wireOp",EDGE,"E2"),sQuery(id+"F0.wireOp",EDGE,"E5.filletArc"),sQuery(id+"F0.wireOp",EDGE,"E6"),sQuery(id+"F0.wireOp",EDGE,"E7"),sQuery(id+"F0.wireOp",EDGE,"E8"),subQ0,sQuery(id+"F0.wireOp",EDGE,"E12.filletArc"),sQuery(id+"F0.wireOp",EDGE,"E13.filletArc"),sQuery(id+"F0.wireOp",EDGE,"E14"),sQuery(id+"F0.wireOp",EDGE,"E15"),sQuery(id+"F0.wireOp",EDGE,"E16.filletArc"),sQuery(id+"F0.wireOp",EDGE,"E19"),sQuery(id+"F0.wireOp",EDGE,"E20"),sQuery(id+"F0.wireOp",EDGE,"E21"),sQuery(id+"F0.wireOp",EDGE,"E22")])],"isStart":true}),makeQuery(id+"F4.opExtrude","CAP_FACE",FACE,{"disambiguationData":[OSD([sQuery(id+"F3.wireOp",EDGE,"E25.0"),sQuery(id+"F3.wireOp",EDGE,"E25.1"),sQuery(id+"F3.wireOp",EDGE,"E25.2"),sQuery(id+"F3.wireOp",EDGE,"E26"),sQuery(id+"F3.wireOp",EDGE,"E27"),sQuery(id+"F3.wireOp",EDGE,"E28.filletArc"),sQuery(id+"F3.wireOp",EDGE,"E29.filletArc"),sQuery(id+"F3.wireOp",EDGE,"E30"),sQuery(id+"F3.wireOp",EDGE,"E31"),sQuery(id+"F3.wireOp",EDGE,"E32.filletArc"),sQuery(id+"F3.wireOp",EDGE,"E33"),sQuery(id+"F3.wireOp",EDGE,"E34")])],"isStart":false})]})]});}
            var Q11;
            {var subQ0=sQuery(id+"F0.wireOp",EDGE,"E7");Q11=makeQuery(id+"F5.opChamfer","BLEND_EDGE",EDGE,{"blendedFrom":[makeQuery(id+"F1.opExtrude","CAP_EDGE",EDGE,{"disambiguationData":[OSD([subQ0])],"isStart":true}),makeQuery(id+"F4.boolean.opBoolean","MERGE",FACE,{"derivedFrom":[makeQuery(id+"F1.opExtrude","CAP_FACE",FACE,{"disambiguationData":[OSD([sQuery(id+"F0.wireOp",EDGE,"E0.left"),sQuery(id+"F0.wireOp",EDGE,"E0.right"),sQuery(id+"F0.wireOp",EDGE,"E1"),sQuery(id+"F0.wireOp",EDGE,"E2"),sQuery(id+"F0.wireOp",EDGE,"E5.filletArc"),sQuery(id+"F0.wireOp",EDGE,"E6"),subQ0,sQuery(id+"F0.wireOp",EDGE,"E8"),sQuery(id+"F0.wireOp",EDGE,"E9"),sQuery(id+"F0.wireOp",EDGE,"E12.filletArc"),sQuery(id+"F0.wireOp",EDGE,"E13.filletArc"),sQuery(id+"F0.wireOp",EDGE,"E14"),sQuery(id+"F0.wireOp",EDGE,"E15"),sQuery(id+"F0.wireOp",EDGE,"E16.filletArc"),sQuery(id+"F0.wireOp",EDGE,"E19"),sQuery(id+"F0.wireOp",EDGE,"E20"),sQuery(id+"F0.wireOp",EDGE,"E21"),sQuery(id+"F0.wireOp",EDGE,"E22")])],"isStart":true}),makeQuery(id+"F4.opExtrude","CAP_FACE",FACE,{"disambiguationData":[OSD([sQuery(id+"F3.wireOp",EDGE,"E25.0"),sQuery(id+"F3.wireOp",EDGE,"E25.1"),sQuery(id+"F3.wireOp",EDGE,"E25.2"),sQuery(id+"F3.wireOp",EDGE,"E26"),sQuery(id+"F3.wireOp",EDGE,"E27"),sQuery(id+"F3.wireOp",EDGE,"E28.filletArc"),sQuery(id+"F3.wireOp",EDGE,"E29.filletArc"),sQuery(id+"F3.wireOp",EDGE,"E30"),sQuery(id+"F3.wireOp",EDGE,"E31"),sQuery(id+"F3.wireOp",EDGE,"E32.filletArc"),sQuery(id+"F3.wireOp",EDGE,"E33"),sQuery(id+"F3.wireOp",EDGE,"E34")])],"isStart":false})]})],"blendedInto":[makeQuery(id+"F4.boolean.opBoolean","MERGE",FACE,{"derivedFrom":[makeQuery(id+"F1.opExtrude","CAP_FACE",FACE,{"disambiguationData":[OSD([sQuery(id+"F0.wireOp",EDGE,"E0.left"),sQuery(id+"F0.wireOp",EDGE,"E0.right"),sQuery(id+"F0.wireOp",EDGE,"E1"),sQuery(id+"F0.wireOp",EDGE,"E2"),sQuery(id+"F0.wireOp",EDGE,"E5.filletArc"),sQuery(id+"F0.wireOp",EDGE,"E6"),subQ0,sQuery(id+"F0.wireOp",EDGE,"E8"),sQuery(id+"F0.wireOp",EDGE,"E9"),sQuery(id+"F0.wireOp",EDGE,"E12.filletArc"),sQuery(id+"F0.wireOp",EDGE,"E13.filletArc"),sQuery(id+"F0.wireOp",EDGE,"E14"),sQuery(id+"F0.wireOp",EDGE,"E15"),sQuery(id+"F0.wireOp",EDGE,"E16.filletArc"),sQuery(id+"F0.wireOp",EDGE,"E19"),sQuery(id+"F0.wireOp",EDGE,"E20"),sQuery(id+"F0.wireOp",EDGE,"E21"),sQuery(id+"F0.wireOp",EDGE,"E22")])],"isStart":true}),makeQuery(id+"F4.opExtrude","CAP_FACE",FACE,{"disambiguationData":[OSD([sQuery(id+"F3.wireOp",EDGE,"E25.0"),sQuery(id+"F3.wireOp",EDGE,"E25.1"),sQuery(id+"F3.wireOp",EDGE,"E25.2"),sQuery(id+"F3.wireOp",EDGE,"E26"),sQuery(id+"F3.wireOp",EDGE,"E27"),sQuery(id+"F3.wireOp",EDGE,"E28.filletArc"),sQuery(id+"F3.wireOp",EDGE,"E29.filletArc"),sQuery(id+"F3.wireOp",EDGE,"E30"),sQuery(id+"F3.wireOp",EDGE,"E31"),sQuery(id+"F3.wireOp",EDGE,"E32.filletArc"),sQuery(id+"F3.wireOp",EDGE,"E33"),sQuery(id+"F3.wireOp",EDGE,"E34")])],"isStart":false})]})]});}
            fillet(context, id + "F10", {"entities" : qUnion([Q0, Q1, Q2, Q3, Q4, Q5, Q6, Q7, Q8, Q9, Q10, Q11]), "tangentPropagation" : true, "radius" : 7 * mm, "defaultsChanged" : true, "vertexSettings" : [], "allowEdgeOverflow" : false});
        }
    });
